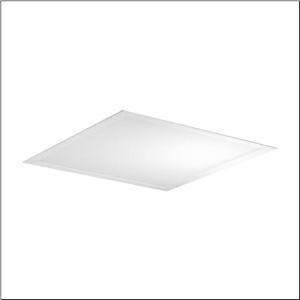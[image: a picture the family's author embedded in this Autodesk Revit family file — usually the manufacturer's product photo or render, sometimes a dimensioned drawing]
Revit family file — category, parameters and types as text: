
# Revit family: apollon_r__31_square_51mp11wd2n42_7747
name_source: partatom
category: Lighting Fixtures
units: mm (PartAtom-declared; Revit-internal decimal feet)

## family parameters
Cut with Voids When Loaded = No
Host = Face
Light Source = No
Part Type = Normal
Room Calculation Point = No
Round Connector Dimension = Use Diameter
Shared = No

## types (1)
- --- (1 x LED, 4000 lm, 27.5 W, 5000K)
    Apparent Load = 28 VA
    CIE Flux Codes = 62 87 97 100 100
    Color Rendering = 80
    Color Temperature = 5000K
    Default Elevation = 1800 mm
    Description = Apollon® 31 square, office luminaire, primary optical cover: micro prismatic cover, of PMMA, CAT 2 (L<= 3000cd/m²), light emission: direct distribution, primary light characteristic: symmetric, installation type: lay-in mounting, LED, rated luminous flux: 4.000lm, luminous efficacy: 145lm/W, light colour: 840/850, colour temperature: 4000/5000K, with terminal, 5-pole, mains connection: 220..240V, AC/DC, 0/50..60Hz, rated input power: 28W, housing, of aluminium, traffic white (RAL 9016), module: M625, length: 620mm, width: 620mm, height: 32mm, housing upper side, of sheet steel, galvanised, protection rating (complete): IP20, protection rating (on room side): IP40, insulation class (complete): insulation class II (safety insulation), certification: CE, ENEC, impact resistance: IK03, permissible operating ambient temperature: -20..+40°C, permissible storage temperature: -20..+60°C, packaging unit: 1 piece
    Height = 0 mm  [stored 0 ft]
    Lamp = 1 x LED
    Lamp Light Flux = 4000 lm
    Lamp Power = 27.5 W
    Lamp count = 1
    Length = 620 mm
    Luminous efficacy = 145 lm/W
    Manufacturer = Siteco
    ModVariant = No
    Model = 51MP11WD2N42
    Mounting Place = Ceiling
    Mounting Type = Recessed
    Number of Poles = 1
    OnlyDefault = Yes
    Power Factor = 1
    Product Name = Apollon® 31 square
    Product group = office luminaire | ceiling recessed
    ProductGroupID = 401
    Protection Class = Protection class II
    Protection Degree = IP 20
    RLX_Detail_Level = 1
    RLX_Emergency_Light_Flux = 0 lm
    RLX_Emergency_Type = 0
    RLX_Emergency_Type_DB = No
    RlxData = <blob elided: 13153 chars, md5=659f3192>
    Socket = socket
    Standby Power = 0 W
    System Light Flux = 4000 lm
    System Power = 28 W
    Type Comments = individual setting: colour temperature 5000K
    Type Image = l_1291039.jpg
    URL = http://relux.com
    VarID = @adj_009001
    Voltage = 0 V
    Weight = 0.00 kg
    Width = 620 mm

note: [stored X ft] marks values corroborated as IEEE doubles in the binary element streams (Revit-internal decimal feet)

## geometry (parser evidence)
native form markers: Sweep x9
no freeform markers — native parametric forms only
